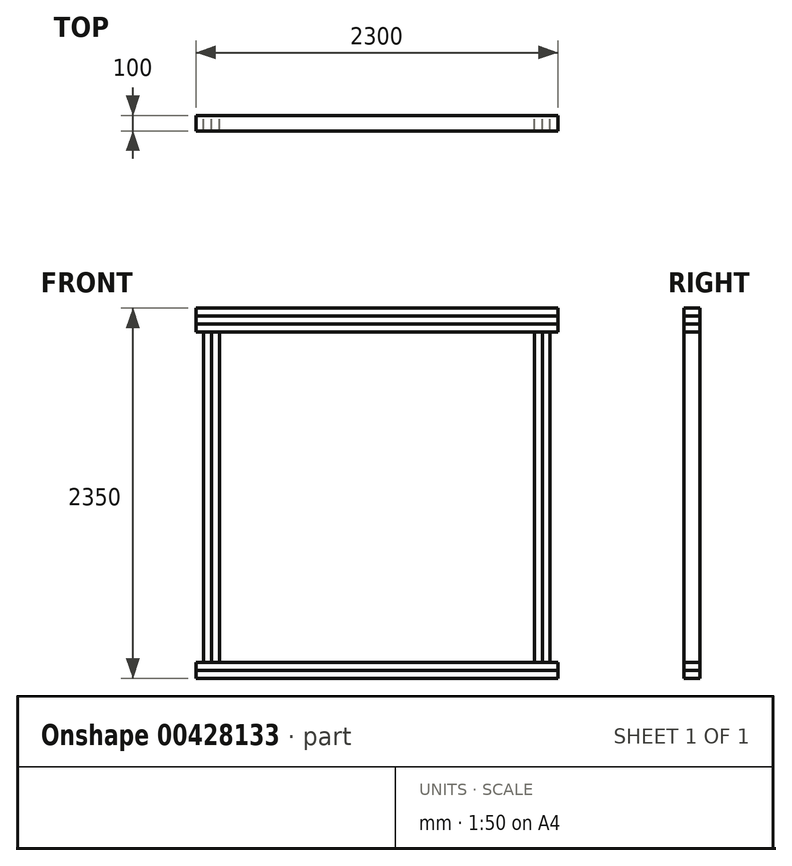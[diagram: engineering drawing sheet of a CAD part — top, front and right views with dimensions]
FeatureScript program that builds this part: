
annotation { "Feature Type Name" : "Feature", "Feature Type Description" : "" }
export const myFeature = defineFeature(function(context is Context, id is Id, definition is map)
    precondition{}
    {
        {
            var Q0;
            Q0=qCreatedBy(makeId("Front.planeOp"),FACE);
            var sketch = newSketch(context, id + "F0", { "sketchPlane" : qUnion([Q0])});
            skLineSegment(sketch, "E0.bottom", {"start": v(-1150, -881.84) * mm, "end": v(1150, -881.84) * mm});
            skLineSegment(sketch, "E0.top", {"start": v(-1150, 1518.16) * mm, "end": v(1150, 1518.16) * mm});
            skLineSegment(sketch, "E0.left", {"start": v(-1150, -881.84) * mm, "end": v(-1150, 1518.16) * mm});
            skLineSegment(sketch, "E0.right", {"start": v(1150, -881.84) * mm, "end": v(1150, 1518.16) * mm});
            skLineSegment(sketch, "E1.top", {"start": v(-1150, -981.84) * mm, "end": v(1150, -981.84) * mm});
            skLineSegment(sketch, "E1.left", {"start": v(-1150, -881.84) * mm, "end": v(-1150, -981.84) * mm});
            skLineSegment(sketch, "E1.right", {"start": v(1150, -881.84) * mm, "end": v(1150, -981.84) * mm});
            skLineSegment(sketch, "E2", {"start": v(-1150, 1518.16) * mm, "end": v(0, 2668.16) * mm});
            skLineSegment(sketch, "E3", {"start": v(0, 2668.16) * mm, "end": v(1150, 1518.16) * mm});
            skLineSegment(sketch, "E4.top", {"start": v(-1150, 1368.16) * mm, "end": v(1150, 1368.16) * mm});
            skLineSegment(sketch, "E4.left", {"start": v(-1150, 1518.16) * mm, "end": v(-1150, 1368.16) * mm});
            skLineSegment(sketch, "E4.right", {"start": v(1150, 1518.16) * mm, "end": v(1150, 1368.16) * mm});
            skLineSegment(sketch, "E5.top", {"start": v(-1150, -731.84) * mm, "end": v(1150, -731.84) * mm});
            skLineSegment(sketch, "E5.left", {"start": v(-1150, -881.84) * mm, "end": v(-1150, -731.84) * mm});
            skLineSegment(sketch, "E5.right", {"start": v(1150, -881.84) * mm, "end": v(1150, -731.84) * mm});
            skLineSegment(sketch, "E6.bottom", {"start": v(-1150, 1368.16) * mm, "end": v(-900, 1368.16) * mm});
            skLineSegment(sketch, "E6.top", {"start": v(-1150, -731.84) * mm, "end": v(-900, -731.84) * mm});
            skLineSegment(sketch, "E6.left", {"start": v(-1150, 1368.16) * mm, "end": v(-1150, -731.84) * mm});
            skLineSegment(sketch, "E6.right", {"start": v(-900, 1368.16) * mm, "end": v(-900, -731.84) * mm});
            skLineSegment(sketch, "E7.bottom", {"start": v(1150, 1368.16) * mm, "end": v(900, 1368.16) * mm});
            skLineSegment(sketch, "E7.top", {"start": v(1150, -731.84) * mm, "end": v(900, -731.84) * mm});
            skLineSegment(sketch, "E7.left", {"start": v(1150, 1368.16) * mm, "end": v(1150, -731.84) * mm});
            skLineSegment(sketch, "E7.right", {"start": v(900, 1368.16) * mm, "end": v(900, -731.84) * mm});
            skLineSegment(sketch, "E8", {"start": v(-1150, -831.84) * mm, "end": v(1150, -831.84) * mm});
            skLineSegment(sketch, "E9", {"start": v(1150, -781.84) * mm, "end": v(-1150, -781.84) * mm});
            skLineSegment(sketch, "E10", {"start": v(-1100, 1368.16) * mm, "end": v(-1100, -731.84) * mm});
            skLineSegment(sketch, "E11", {"start": v(-1050, 1368.16) * mm, "end": v(-1050, -731.84) * mm});
            skLineSegment(sketch, "E12", {"start": v(-1000, 1368.16) * mm, "end": v(-1000, -731.84) * mm});
            skLineSegment(sketch, "E13", {"start": v(-950, 1368.16) * mm, "end": v(-950, -731.84) * mm});
            skLineSegment(sketch, "E14", {"start": v(-1150, 1418.16) * mm, "end": v(1150, 1418.16) * mm});
            skLineSegment(sketch, "E15", {"start": v(-1150, 1468.16) * mm, "end": v(1150, 1468.16) * mm});
            skLineSegment(sketch, "E16", {"start": v(0, -981.84) * mm, "end": v(0, -1457.66) * mm, "construction": true});
            skLineSegment(sketch, "E17.MirrorCS", {"start": v(950, 1368.16) * mm, "end": v(950, -731.84) * mm});
            skLineSegment(sketch, "E18.MirrorCS", {"start": v(1000, 1368.16) * mm, "end": v(1000, -731.84) * mm});
            skLineSegment(sketch, "E19.MirrorCS", {"start": v(1100, 1368.16) * mm, "end": v(1100, -731.84) * mm});
            skLineSegment(sketch, "E20.MirrorCS", {"start": v(1050, 1368.16) * mm, "end": v(1050, -731.84) * mm});
            skLineSegment(sketch, "E21", {"start": v(0, 1518.16) * mm, "end": v(0, 2668.16) * mm});
            skPoint(sketch, "E22", {"position": v(-50, 1518.16) * mm});
            skLineSegment(sketch, "E23", {"start": v(-1079.29, 1518.16) * mm, "end": v(0, 2597.45) * mm});
            skLineSegment(sketch, "E24", {"start": v(-1023.94, 1518.16) * mm, "end": v(0, 2542.1) * mm});
            skSolve(sketch);
        }
        {
            var Q0;
            {var subQ0=sQuery(id+"F0.wireOp",EDGE,"E14");Q0=makeQuery(id+"F0.imprint","IMPRINT",FACE,{"disambiguationData":[TD([[makeQuery(id+"F0.imprint","IMPRINT",EDGE,{"derivedFrom":subQ0}),1.0]])]});}
            var Q1;
            {var subQ0=sQuery(id+"F0.wireOp",EDGE,"E6.left");Q1=makeQuery(id+"F0.imprint","IMPRINT",FACE,{"disambiguationData":[TD([[makeQuery(id+"F0.imprint","IMPRINT",EDGE,{"derivedFrom":subQ0}),1.0]])]});}
            var Q2;
            {var subQ0=sQuery(id+"F0.wireOp",EDGE,"E11");Q2=makeQuery(id+"F0.imprint","IMPRINT",FACE,{"disambiguationData":[TD([[makeQuery(id+"F0.imprint","IMPRINT",EDGE,{"derivedFrom":subQ0}),1.0]])]});}
            var Q3;
            {var subQ0=sQuery(id+"F0.wireOp",EDGE,"E8");Q3=makeQuery(id+"F0.imprint","IMPRINT",FACE,{"disambiguationData":[TD([[makeQuery(id+"F0.imprint","IMPRINT",EDGE,{"derivedFrom":subQ0}),1.0]])]});}
            var Q4;
            {var subQ0=sQuery(id+"F0.wireOp",EDGE,"E7.left");Q4=makeQuery(id+"F0.imprint","IMPRINT",FACE,{"disambiguationData":[TD([[makeQuery(id+"F0.imprint","IMPRINT",EDGE,{"derivedFrom":subQ0}),-1.0]])]});}
            var Q5;
            {var subQ0=sQuery(id+"F0.wireOp",EDGE,"E18.MirrorCS");Q5=makeQuery(id+"F0.imprint","IMPRINT",FACE,{"disambiguationData":[TD([[makeQuery(id+"F0.imprint","IMPRINT",EDGE,{"derivedFrom":subQ0}),1.0]])]});}
            extrude(context, id + "F1", {"entities" : qUnion([Q0, Q1, Q2, Q3, Q4, Q5]), "depth" : 100 * mm});
        }
        {
            var Q0;
            {var subQ8=sQuery(id+"F0.wireOp",EDGE,"E15");Q0=makeQuery(id+"F0.imprint","IMPRINT",FACE,{"disambiguationData":[TD([[makeQuery(id+"F0.imprint","IMPRINT",EDGE,{"derivedFrom":subQ8}),1.0]])]});}
            var Q1;
            {var subQ1=sQuery(id+"F0.wireOp",EDGE,"E4.top");Q1=makeQuery(id+"F0.imprint","IMPRINT",FACE,{"disambiguationData":[TD([[makeQuery(id+"F0.imprint","IMPRINT",EDGE,{"derivedFrom":subQ1}),1.0]])]});}
            var Q2;
            {var subQ1=sQuery(id+"F0.wireOp",EDGE,"E5.top");Q2=makeQuery(id+"F0.imprint","IMPRINT",FACE,{"disambiguationData":[TD([[makeQuery(id+"F0.imprint","IMPRINT",EDGE,{"derivedFrom":subQ1}),-1.0]])]});}
            var Q3;
            {var subQ0=sQuery(id+"F0.wireOp",EDGE,"E0.bottom");Q3=makeQuery(id+"F0.imprint","IMPRINT",FACE,{"disambiguationData":[TD([[makeQuery(id+"F0.imprint","IMPRINT",EDGE,{"derivedFrom":subQ0}),1.0]])]});}
            extrude(context, id + "F2", {"entities" : qUnion([Q0, Q1, Q2, Q3]), "depth" : 100 * mm});
        }
        {
            var Q0;
            {var subQ0=sQuery(id+"F0.wireOp",EDGE,"E10");Q0=makeQuery(id+"F0.imprint","IMPRINT",FACE,{"disambiguationData":[TD([[makeQuery(id+"F0.imprint","IMPRINT",EDGE,{"derivedFrom":subQ0}),1.0]])]});}
            var Q1;
            {var subQ0=sQuery(id+"F0.wireOp",EDGE,"E19.MirrorCS");Q1=makeQuery(id+"F0.imprint","IMPRINT",FACE,{"disambiguationData":[TD([[makeQuery(id+"F0.imprint","IMPRINT",EDGE,{"derivedFrom":subQ0}),-1.0]])]});}
            extrude(context, id + "F3", {"entities" : qUnion([Q0, Q1]), "depth" : 100 * mm});
        }
    });
